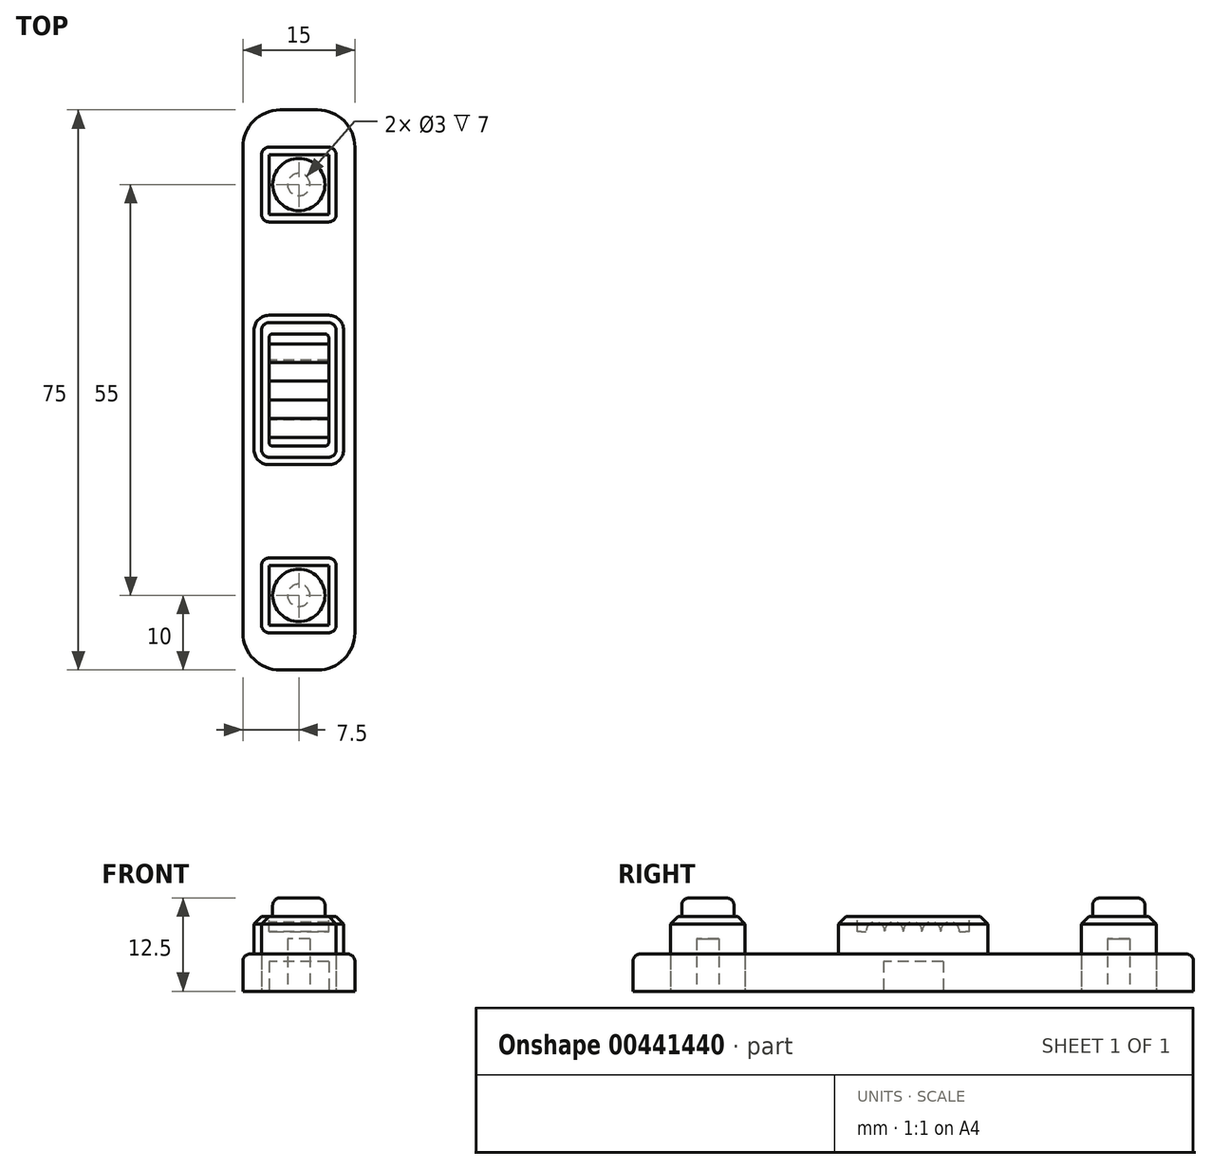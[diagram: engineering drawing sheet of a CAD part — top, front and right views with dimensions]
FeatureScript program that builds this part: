
annotation { "Feature Type Name" : "Feature", "Feature Type Description" : "" }
export const myFeature = defineFeature(function(context is Context, id is Id, definition is map)
    precondition{}
    {
        {
            var Q0;
            Q0=qCreatedBy(makeId("Top.planeOp"),FACE);
            var sketch = newSketch(context, id + "F0", { "sketchPlane" : qUnion([Q0])});
            skLineSegment(sketch, "E0.bottom", {"start": v(5, -5) * mm, "end": v(-5, -5) * mm});
            skLineSegment(sketch, "E0.top", {"start": v(5, 5) * mm, "end": v(-5, 5) * mm});
            skLineSegment(sketch, "E0.left", {"start": v(5, -5) * mm, "end": v(5, 5) * mm});
            skLineSegment(sketch, "E0.right", {"start": v(-5, -5) * mm, "end": v(-5, 5) * mm});
            skPoint(sketch, "E0.middle", {"position": v(0, 0) * mm});
            skSolve(sketch);
        }
        {
            var Q0;
            Q0 = qSketchRegion(id + "F0", true);
            extrude(context, id + "F1", {"entities" : qUnion([Q0]), "depth" : 10 * mm});
        }
        {
            var Q0;
            Q0=qCreatedBy(makeId("Top.planeOp"),FACE);
            var sketch = newSketch(context, id + "F2", { "sketchPlane" : qUnion([Q0])});
            skCircle(sketch, "E1", {"center": v(0, 0) * mm, "radius": 1.5 * mm});
            skSolve(sketch);
        }
        {
            var Q0;
            Q0 = qSketchRegion(id + "F2", true);
            extrude(context, id + "F3", {"entities" : qUnion([Q0]), "operationType" : NewBodyOperationType.REMOVE, "depth" : 7 * mm});
        }
        {
            var Q0;
            Q0=makeQuery(id+"F1.opExtrude","SWEPT_EDGE",EDGE,{"disambiguationData":[OSD([sQuery(id+"F0.wireOp",EDGE,"E0.bottom"),sQuery(id+"F0.wireOp",EDGE,"E0.right")])]});
            var Q1;
            Q1=makeQuery(id+"F1.opExtrude","SWEPT_EDGE",EDGE,{"disambiguationData":[OSD([sQuery(id+"F0.wireOp",EDGE,"E0.top"),sQuery(id+"F0.wireOp",EDGE,"E0.right")])]});
            var Q2;
            Q2=makeQuery(id+"F1.opExtrude","SWEPT_EDGE",EDGE,{"disambiguationData":[OSD([sQuery(id+"F0.wireOp",EDGE,"E0.bottom"),sQuery(id+"F0.wireOp",EDGE,"E0.left")])]});
            var Q3;
            Q3=makeQuery(id+"F1.opExtrude","SWEPT_EDGE",EDGE,{"disambiguationData":[OSD([sQuery(id+"F0.wireOp",EDGE,"E0.top"),sQuery(id+"F0.wireOp",EDGE,"E0.left")])]});
            fillet(context, id + "F4", {"entities" : qUnion([Q0, Q1, Q2, Q3]), "radius" : 1 * mm, "tangentPropagation" : true, "allowEdgeOverflow" : false});
        }
        {
            var Q0;
            Q0=makeQuery(id+"F1.opExtrude","CAP_FACE",FACE,{"disambiguationData":[OSD([sQuery(id+"F0.wireOp",EDGE,"E0.bottom"),sQuery(id+"F0.wireOp",EDGE,"E0.top"),sQuery(id+"F0.wireOp",EDGE,"E0.left"),sQuery(id+"F0.wireOp",EDGE,"E0.right")])],"isStart":false});
            var sketch = newSketch(context, id + "F5", { "sketchPlane" : qUnion([Q0])});
            skCircle(sketch, "E2", {"center": v(0, 0) * mm, "radius": 3.5 * mm});
            skSolve(sketch);
        }
        {
            var Q0;
            Q0 = qSketchRegion(id + "F5", true);
            extrude(context, id + "F6", {"entities" : qUnion([Q0]), "operationType" : NewBodyOperationType.ADD, "depth" : 2.5 * mm});
        }
        {
            var Q0;
            Q0=makeQuery(id+"F6.opExtrude","CAP_EDGE",EDGE,{"disambiguationData":[OSD([sQuery(id+"F5.wireOp",EDGE,"E2")])],"isStart":false});
            fillet(context, id + "F7", {"entities" : qUnion([Q0]), "radius" : 1 * mm, "tangentPropagation" : true, "allowEdgeOverflow" : false});
        }
        {
            var Q0;
            Q0=makeQuery(id+"F1.opExtrude","SWEPT_BODY",BODY,{"disambiguationData":[OSD([sQuery(id+"F0.wireOp",EDGE,"E0.bottom"),sQuery(id+"F0.wireOp",EDGE,"E0.top"),sQuery(id+"F0.wireOp",EDGE,"E0.left"),sQuery(id+"F0.wireOp",EDGE,"E0.right")])]});
            var Q1;
            Q1=qCreatedBy(makeId("Front.planeOp"),FACE);
            transform(context, id + "F8", {"entities" : qUnion([Q0]), "transformType" : TransformType.TRANSLATION_DISTANCE, "transformDirection" : qUnion([Q1]), "distance" : 55 * mm, "makeCopy" : true});
        }
        {
            var Q0;
            Q0=makeQuery(id+"F8.opPattern","COPY",BODY,{"derivedFrom":makeQuery(id+"F1.opExtrude","SWEPT_BODY",BODY,{"disambiguationData":[OSD([sQuery(id+"F0.wireOp",EDGE,"E0.bottom"),sQuery(id+"F0.wireOp",EDGE,"E0.top"),sQuery(id+"F0.wireOp",EDGE,"E0.left"),sQuery(id+"F0.wireOp",EDGE,"E0.right")])]}),"instanceName":"1"});
            var Q1;
            Q1=makeQuery(id+"F1.opExtrude","SWEPT_BODY",BODY,{"disambiguationData":[OSD([sQuery(id+"F0.wireOp",EDGE,"E0.bottom"),sQuery(id+"F0.wireOp",EDGE,"E0.top"),sQuery(id+"F0.wireOp",EDGE,"E0.left"),sQuery(id+"F0.wireOp",EDGE,"E0.right")])]});
            transform(context, id + "F9", {"entities" : qUnion([Q0, Q1]), "transformType" : TransformType.TRANSLATION_3D, "dx" : 0 * mm, "dy" : 27.5 * mm, "dz" : 0 * mm, "makeCopy" : false});
        }
        {
            var Q0;
            Q0=qCreatedBy(makeId("Top.planeOp"),FACE);
            var sketch = newSketch(context, id + "F10", { "sketchPlane" : qUnion([Q0])});
            skLineSegment(sketch, "E3.bottom", {"start": v(-2.5, -37.5) * mm, "end": v(2.5, -37.5) * mm});
            skLineSegment(sketch, "E3.top", {"start": v(-2.5, 37.5) * mm, "end": v(2.5, 37.5) * mm});
            skLineSegment(sketch, "E3.left", {"start": v(-7.5, -32.5) * mm, "end": v(-7.5, 32.5) * mm});
            skLineSegment(sketch, "E3.right", {"start": v(7.5, -32.5) * mm, "end": v(7.5, 32.5) * mm});
            skPoint(sketch, "E3.middle", {"position": v(0, 0) * mm});
            skPoint(sketch, "E4.visualSharp", {"position": v(7.5, 37.5) * mm});
            skArc(sketch, "E4.filletArc", {"start": v(7.5, 32.5) * mm, "mid": v(6.04, 36.04) * mm, "end": v(2.5, 37.5) * mm});
            skPoint(sketch, "E5.visualSharp", {"position": v(-7.5, 37.5) * mm});
            skArc(sketch, "E5.filletArc", {"start": v(-2.5, 37.5) * mm, "mid": v(-6.04, 36.04) * mm, "end": v(-7.5, 32.5) * mm});
            skPoint(sketch, "E6.visualSharp", {"position": v(-7.5, -37.5) * mm});
            skArc(sketch, "E6.filletArc", {"start": v(-7.5, -32.5) * mm, "mid": v(-6.04, -36.04) * mm, "end": v(-2.5, -37.5) * mm});
            skPoint(sketch, "E7.visualSharp", {"position": v(7.5, -37.5) * mm});
            skArc(sketch, "E7.filletArc", {"start": v(2.5, -37.5) * mm, "mid": v(6.04, -36.04) * mm, "end": v(7.5, -32.5) * mm});
            skSolve(sketch);
        }
        {
            var Q0;
            Q0 = qSketchRegion(id + "F10", true);
            extrude(context, id + "F11", {"entities" : qUnion([Q0]), "depth" : 5 * mm});
        }
        {
            var Q0;
            Q0=makeQuery(id+"F11.opExtrude","CAP_EDGE",EDGE,{"disambiguationData":[OSD([sQuery(id+"F10.wireOp",EDGE,"E3.left")])],"isStart":false});
            fillet(context, id + "F12", {"entities" : qUnion([Q0]), "radius" : 1 * mm, "tangentPropagation" : true, "allowEdgeOverflow" : false});
        }
        {
            var Q0;
            Q0=makeQuery(id+"F11.opExtrude","CAP_FACE",FACE,{"disambiguationData":[OSD([sQuery(id+"F10.wireOp",EDGE,"E3.bottom"),sQuery(id+"F10.wireOp",EDGE,"E3.top"),sQuery(id+"F10.wireOp",EDGE,"E3.left"),sQuery(id+"F10.wireOp",EDGE,"E3.right"),sQuery(id+"F10.wireOp",EDGE,"E4.filletArc"),sQuery(id+"F10.wireOp",EDGE,"E5.filletArc"),sQuery(id+"F10.wireOp",EDGE,"E6.filletArc"),sQuery(id+"F10.wireOp",EDGE,"E7.filletArc")])],"isStart":false});
            var sketch = newSketch(context, id + "F13", { "sketchPlane" : qUnion([Q0])});
            skLineSegment(sketch, "E8.bottom", {"start": v(-4, 10) * mm, "end": v(4, 10) * mm});
            skLineSegment(sketch, "E8.top", {"start": v(-4, -10) * mm, "end": v(4, -10) * mm});
            skLineSegment(sketch, "E8.left", {"start": v(-6, 8) * mm, "end": v(-6, -8) * mm});
            skLineSegment(sketch, "E8.right", {"start": v(6, 8) * mm, "end": v(6, -8) * mm});
            skPoint(sketch, "E8.middle", {"position": v(0, 0) * mm});
            skPoint(sketch, "E9.visualSharp", {"position": v(-6, -10) * mm});
            skArc(sketch, "E9.filletArc", {"start": v(-6, -8) * mm, "mid": v(-5.41, -9.41) * mm, "end": v(-4, -10) * mm});
            skPoint(sketch, "E10.visualSharp", {"position": v(-6, 10) * mm});
            skArc(sketch, "E10.filletArc", {"start": v(-4, 10) * mm, "mid": v(-5.41, 9.41) * mm, "end": v(-6, 8) * mm});
            skPoint(sketch, "E11.visualSharp", {"position": v(6, 10) * mm});
            skArc(sketch, "E11.filletArc", {"start": v(6, 8) * mm, "mid": v(5.41, 9.41) * mm, "end": v(4, 10) * mm});
            skPoint(sketch, "E12.visualSharp", {"position": v(6, -10) * mm});
            skArc(sketch, "E12.filletArc", {"start": v(4, -10) * mm, "mid": v(5.41, -9.41) * mm, "end": v(6, -8) * mm});
            skSolve(sketch);
        }
        {
            var Q0;
            Q0 = qSketchRegion(id + "F13", true);
            extrude(context, id + "F14", {"entities" : qUnion([Q0]), "operationType" : NewBodyOperationType.ADD, "depth" : 5 * mm});
        }
        {
            var Q0;
            Q0=makeQuery(id+"F14.opExtrude","CAP_FACE",FACE,{"disambiguationData":[OSD([sQuery(id+"F13.wireOp",EDGE,"E8.bottom"),sQuery(id+"F13.wireOp",EDGE,"E8.top"),sQuery(id+"F13.wireOp",EDGE,"E8.left"),sQuery(id+"F13.wireOp",EDGE,"E8.right"),sQuery(id+"F13.wireOp",EDGE,"E9.filletArc"),sQuery(id+"F13.wireOp",EDGE,"E10.filletArc"),sQuery(id+"F13.wireOp",EDGE,"E11.filletArc"),sQuery(id+"F13.wireOp",EDGE,"E12.filletArc")])],"isStart":false});
            var sketch = newSketch(context, id + "F15", { "sketchPlane" : qUnion([Q0])});
            skLineSegment(sketch, "E13.bottom", {"start": v(-3.5, -7.5) * mm, "end": v(3.5, -7.5) * mm});
            skLineSegment(sketch, "E13.top", {"start": v(-3.5, 7.5) * mm, "end": v(3.5, 7.5) * mm});
            skLineSegment(sketch, "E13.left", {"start": v(-4, -7) * mm, "end": v(-4, 7) * mm});
            skLineSegment(sketch, "E13.right", {"start": v(4, -7) * mm, "end": v(4, 7) * mm});
            skPoint(sketch, "E13.middle", {"position": v(0, 0) * mm});
            skPoint(sketch, "E14.visualSharp", {"position": v(-4, -7.5) * mm});
            skArc(sketch, "E14.filletArc", {"start": v(-4, -7) * mm, "mid": v(-3.85, -7.35) * mm, "end": v(-3.5, -7.5) * mm});
            skPoint(sketch, "E15.visualSharp", {"position": v(-4, 7.5) * mm});
            skArc(sketch, "E15.filletArc", {"start": v(-3.5, 7.5) * mm, "mid": v(-3.85, 7.35) * mm, "end": v(-4, 7) * mm});
            skPoint(sketch, "E16.visualSharp", {"position": v(4, 7.5) * mm});
            skArc(sketch, "E16.filletArc", {"start": v(4, 7) * mm, "mid": v(3.85, 7.35) * mm, "end": v(3.5, 7.5) * mm});
            skPoint(sketch, "E17.visualSharp", {"position": v(4, -7.5) * mm});
            skArc(sketch, "E17.filletArc", {"start": v(3.5, -7.5) * mm, "mid": v(3.85, -7.35) * mm, "end": v(4, -7) * mm});
            skSolve(sketch);
        }
        {
            var Q0;
            Q0 = qSketchRegion(id + "F15", true);
            extrude(context, id + "F16", {"entities" : qUnion([Q0]), "operationType" : NewBodyOperationType.REMOVE, "oppositeDirection" : true, "depth" : 2 * mm});
        }
        {
            var Q0;
            Q0=makeQuery(id+"F16.boolean.opBoolean","COPY",FACE,{"derivedFrom":makeQuery(id+"F16.opExtrude","SWEPT_FACE",FACE,{"disambiguationData":[OSD([sQuery(id+"F15.wireOp",EDGE,"E13.left")])]})});
            var sketch = newSketch(context, id + "F17", { "sketchPlane" : qUnion([Q0])});
            skCircle(sketch, "E18", {"center": v(-5.08, 8) * mm, "radius": 1.25 * mm});
            skCircle(sketch, "E19.1.0.0", {"center": v(-2.58, 8) * mm, "radius": 1.25 * mm});
            skCircle(sketch, "E19.2.0.0", {"center": v(-0.08, 8) * mm, "radius": 1.25 * mm});
            skCircle(sketch, "E19.3.0.0", {"center": v(2.42, 8) * mm, "radius": 1.25 * mm});
            skCircle(sketch, "E19.4.0.0", {"center": v(4.92, 8) * mm, "radius": 1.25 * mm});
            skLineSegment(sketch, "E19.direction1", {"start": v(-5.08, 8) * mm, "end": v(-2.58, 8) * mm, "construction": true});
            skSolve(sketch);
        }
        {
            var Q0;
            {var subQ0=sQuery(id+"F17.wireOp",EDGE,"E18");var subQ1=sQuery(id+"F15.wireOp",EDGE,"E13.left");var subQ2=makeQuery(id+"F16.boolean.opBoolean","COPY",EDGE,{"derivedFrom":makeQuery(id+"F16.opExtrude","SWEPT_EDGE",EDGE,{"disambiguationData":[OSD([subQ1,sQuery(id+"F15.wireOp",EDGE,"E14.filletArc")])]})});var subQ3=makeQuery(id+"F17.imprint","INTERSECT",VERTEX,{"derivedFrom":[subQ2,subQ0]});Q0=makeQuery(id+"F17.imprint","IMPRINT",FACE,{"disambiguationData":[TD([[makeQuery(id+"F17.imprint","IMPRINT",EDGE,{"disambiguationData":[TD([[subQ3,1.0]])],"derivedFrom":subQ0}),1.0]])]});}
            var Q1;
            {var subQ0=sQuery(id+"F17.wireOp",EDGE,"E19.1.0.0");var subQ1=makeQuery(id+"F16.boolean.opBoolean","COPY",EDGE,{"derivedFrom":makeQuery(id+"F16.opExtrude","CAP_EDGE",EDGE,{"disambiguationData":[OSD([sQuery(id+"F15.wireOp",EDGE,"E13.left")])],"isStart":false})});var subQ2=makeQuery(id+"F17.imprint","INTERSECT",VERTEX,{"derivedFrom":[subQ1,sQuery(id+"F17.wireOp",EDGE,"E18"),subQ0]});Q1=makeQuery(id+"F17.imprint","IMPRINT",FACE,{"disambiguationData":[TD([[makeQuery(id+"F17.imprint","IMPRINT",EDGE,{"disambiguationData":[TD([[subQ2,1.0]])],"derivedFrom":subQ0}),1.0]])]});}
            var Q2;
            {var subQ0=sQuery(id+"F17.wireOp",EDGE,"E19.2.0.0");var subQ1=makeQuery(id+"F16.boolean.opBoolean","COPY",EDGE,{"derivedFrom":makeQuery(id+"F16.opExtrude","CAP_EDGE",EDGE,{"disambiguationData":[OSD([sQuery(id+"F15.wireOp",EDGE,"E13.left")])],"isStart":false})});var subQ2=makeQuery(id+"F17.imprint","INTERSECT",VERTEX,{"derivedFrom":[subQ1,sQuery(id+"F17.wireOp",EDGE,"E19.1.0.0"),subQ0]});Q2=makeQuery(id+"F17.imprint","IMPRINT",FACE,{"disambiguationData":[TD([[makeQuery(id+"F17.imprint","IMPRINT",EDGE,{"disambiguationData":[TD([[subQ2,1.0]])],"derivedFrom":subQ0}),1.0]])]});}
            var Q3;
            {var subQ0=sQuery(id+"F17.wireOp",EDGE,"E19.3.0.0");var subQ1=makeQuery(id+"F16.boolean.opBoolean","COPY",EDGE,{"derivedFrom":makeQuery(id+"F16.opExtrude","CAP_EDGE",EDGE,{"disambiguationData":[OSD([sQuery(id+"F15.wireOp",EDGE,"E13.left")])],"isStart":false})});var subQ2=makeQuery(id+"F17.imprint","INTERSECT",VERTEX,{"derivedFrom":[subQ1,sQuery(id+"F17.wireOp",EDGE,"E19.2.0.0"),subQ0]});Q3=makeQuery(id+"F17.imprint","IMPRINT",FACE,{"disambiguationData":[TD([[makeQuery(id+"F17.imprint","IMPRINT",EDGE,{"disambiguationData":[TD([[subQ2,1.0]])],"derivedFrom":subQ0}),1.0]])]});}
            var Q4;
            {var subQ0=sQuery(id+"F17.wireOp",EDGE,"E19.4.0.0");var subQ1=sQuery(id+"F15.wireOp",EDGE,"E13.left");var subQ2=makeQuery(id+"F16.boolean.opBoolean","COPY",EDGE,{"derivedFrom":makeQuery(id+"F16.opExtrude","SWEPT_EDGE",EDGE,{"disambiguationData":[OSD([subQ1,sQuery(id+"F15.wireOp",EDGE,"E15.filletArc")])]})});var subQ3=makeQuery(id+"F17.imprint","INTERSECT",VERTEX,{"derivedFrom":[subQ2,subQ0]});Q4=makeQuery(id+"F17.imprint","IMPRINT",FACE,{"disambiguationData":[TD([[makeQuery(id+"F17.imprint","IMPRINT",EDGE,{"disambiguationData":[TD([[subQ3,-1.0]])],"derivedFrom":subQ0}),1.0]])]});}
            var Q5;
            Q5=sQuery(id+"F17.wireOp",EDGE,"E18");
            var Q6;
            Q6=sQuery(id+"F17.wireOp",EDGE,"E19.1.0.0");
            var Q7;
            Q7=sQuery(id+"F17.wireOp",EDGE,"E19.2.0.0");
            var Q8;
            Q8=sQuery(id+"F17.wireOp",EDGE,"E19.3.0.0");
            var Q9;
            Q9=sQuery(id+"F17.wireOp",EDGE,"E19.4.0.0");
            extrude(context, id + "F18", {"entities" : qUnion([Q0, Q1, Q2, Q3, Q4]), "operationType" : NewBodyOperationType.ADD, "surfaceEntities" : qUnion([Q5, Q6, Q7, Q8, Q9]), "depth" : 8 * mm});
        }
        {
            var Q0;
            Q0=makeQuery(id+"F8.opPattern","COPY",EDGE,{"derivedFrom":makeQuery(id+"F1.opExtrude","CAP_EDGE",EDGE,{"disambiguationData":[OSD([sQuery(id+"F0.wireOp",EDGE,"E0.right")])],"isStart":false}),"instanceName":"1"});
            var Q1;
            Q1=makeQuery(id+"F1.opExtrude","CAP_EDGE",EDGE,{"disambiguationData":[OSD([sQuery(id+"F0.wireOp",EDGE,"E0.right")])],"isStart":false});
            var Q2;
            Q2=makeQuery(id+"F14.opExtrude","CAP_EDGE",EDGE,{"disambiguationData":[OSD([sQuery(id+"F13.wireOp",EDGE,"E8.left")])],"isStart":false});
            chamfer(context, id + "F19", {"entities" : qUnion([Q0, Q1, Q2]), "width" : 1 * mm, "tangentPropagation" : true});
        }
        {
            var Q0;
            Q0=makeQuery(id+"F11.opExtrude","CAP_FACE",FACE,{"disambiguationData":[OSD([sQuery(id+"F10.wireOp",EDGE,"E3.bottom"),sQuery(id+"F10.wireOp",EDGE,"E3.top"),sQuery(id+"F10.wireOp",EDGE,"E3.left"),sQuery(id+"F10.wireOp",EDGE,"E3.right"),sQuery(id+"F10.wireOp",EDGE,"E4.filletArc"),sQuery(id+"F10.wireOp",EDGE,"E5.filletArc"),sQuery(id+"F10.wireOp",EDGE,"E6.filletArc"),sQuery(id+"F10.wireOp",EDGE,"E7.filletArc")])],"isStart":true});
            var sketch = newSketch(context, id + "F20", { "sketchPlane" : qUnion([Q0])});
            skLineSegment(sketch, "E20.bottom", {"start": v(4, -4) * mm, "end": v(-4, -4) * mm});
            skLineSegment(sketch, "E20.top", {"start": v(4, 4) * mm, "end": v(-4, 4) * mm});
            skLineSegment(sketch, "E20.left", {"start": v(4, -4) * mm, "end": v(4, 4) * mm});
            skLineSegment(sketch, "E20.right", {"start": v(-4, -4) * mm, "end": v(-4, 4) * mm});
            skPoint(sketch, "E20.middle", {"position": v(0, 0) * mm});
            skSolve(sketch);
        }
        {
            var Q0;
            Q0 = qSketchRegion(id + "F20", true);
            extrude(context, id + "F21", {"entities" : qUnion([Q0]), "operationType" : NewBodyOperationType.REMOVE, "oppositeDirection" : true, "depth" : 4 * mm});
        }
    });
